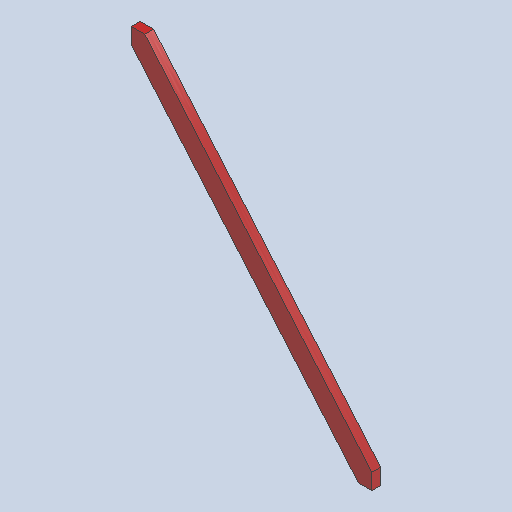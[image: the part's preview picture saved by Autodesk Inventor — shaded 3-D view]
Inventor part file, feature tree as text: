
AUTODESK INVENTOR PART (.ipt)
format: ipt  version: 2025 (Build 290162000, 162)  size: 95,232 bytes
history: native  units: in
note: dims shown in document units (in); Inventor stores cm internally (conversion verified against a paired STEP export)
features: other x4, sketch x1
ambient origin geometry x8: Origin, YZ Plane, XZ Plane, XY Plane, X Axis, Y Axis, Z Axis, Center Point
bodies: Solid1 (feature_tree)
feature tree (5):
  other  "44x2x4.ipt"
  other  "Solid1::44x2x4.ipt"
  other  "TaggingFeature1"
  sketch  "Sketch1"  dims[d0=0.3937in]
  other  "Finish1"
